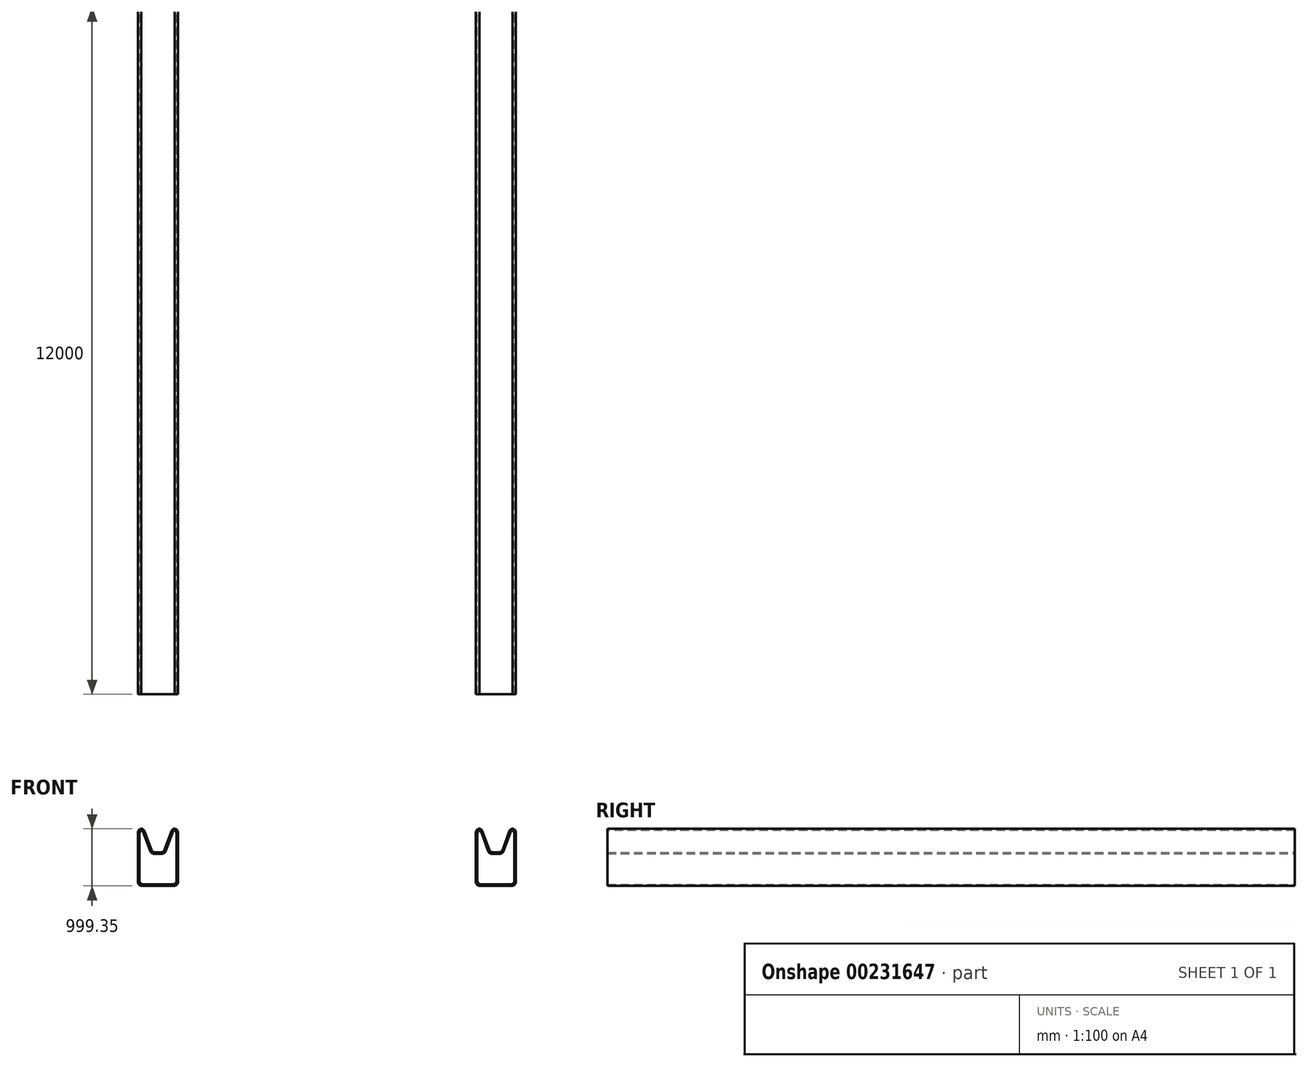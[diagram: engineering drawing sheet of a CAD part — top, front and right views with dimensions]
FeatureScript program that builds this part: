
annotation { "Feature Type Name" : "Feature", "Feature Type Description" : "" }
export const myFeature = defineFeature(function(context is Context, id is Id, definition is map)
    precondition{}
    {
        {
            var Q0;
            Q0=qCreatedBy(makeId("Front.planeOp"),FACE);
            var sketch = newSketch(context, id + "F0", { "sketchPlane" : qUnion([Q0])});
            skLineSegment(sketch, "E0.bottom", {"start": v(2600, 500) * mm, "end": v(2700, 500) * mm});
            skLineSegment(sketch, "E0.top", {"start": v(2600, -500) * mm, "end": v(3300, -500) * mm});
            skLineSegment(sketch, "E0.left", {"start": v(2600, 500) * mm, "end": v(2600, 200) * mm});
            skLineSegment(sketch, "E0.right", {"start": v(3300, 500) * mm, "end": v(3300, -500) * mm});
            skLineSegment(sketch, "E1", {"start": v(0, 0) * mm, "end": v(0, 1224.09) * mm, "construction": true});
            skLineSegment(sketch, "E2", {"start": v(2600, 200) * mm, "end": v(2600, 0) * mm});
            skLineSegment(sketch, "E3", {"start": v(2600, 0) * mm, "end": v(2600, -200) * mm});
            skLineSegment(sketch, "E4", {"start": v(2600, -200) * mm, "end": v(2600, -200) * mm});
            skLineSegment(sketch, "E5.trimOffspring", {"start": v(2600, -200) * mm, "end": v(2600, -500) * mm});
            skLineSegment(sketch, "E6", {"start": v(2700, 500) * mm, "end": v(2850, 87.88) * mm});
            skLineSegment(sketch, "E7", {"start": v(2850, 87.88) * mm, "end": v(3050, 87.88) * mm});
            skLineSegment(sketch, "E8", {"start": v(3050, 87.88) * mm, "end": v(3200, 500) * mm});
            skLineSegment(sketch, "E9.trimOffspring", {"start": v(3200, 500) * mm, "end": v(3300, 500) * mm});
            skLineSegment(sketch, "E10.MirrorCS", {"start": v(-2600, 0) * mm, "end": v(-2600, -200) * mm});
            skLineSegment(sketch, "E11.MirrorCS", {"start": v(-3200, 500) * mm, "end": v(-3300, 500) * mm});
            skLineSegment(sketch, "E12.MirrorCS", {"start": v(-3050, 87.88) * mm, "end": v(-3200, 500) * mm});
            skLineSegment(sketch, "E13.MirrorCS", {"start": v(-2850, 87.88) * mm, "end": v(-3050, 87.88) * mm});
            skLineSegment(sketch, "E14.MirrorCS", {"start": v(-2700, 500) * mm, "end": v(-2850, 87.88) * mm});
            skLineSegment(sketch, "E15.MirrorCS", {"start": v(-2600, 200) * mm, "end": v(-2600, 0) * mm});
            skLineSegment(sketch, "E16.MirrorCS", {"start": v(-2600, 500) * mm, "end": v(-2700, 500) * mm});
            skLineSegment(sketch, "E17.MirrorCS", {"start": v(-2600, -200) * mm, "end": v(-2600, -500) * mm});
            skLineSegment(sketch, "E18.MirrorCS", {"start": v(-3300, 500) * mm, "end": v(-3300, -500) * mm});
            skLineSegment(sketch, "E19.MirrorCS", {"start": v(-2600, -500) * mm, "end": v(-3300, -500) * mm});
            skLineSegment(sketch, "E20.MirrorCS", {"start": v(-2600, 500) * mm, "end": v(-2600, 200) * mm});
            skSolve(sketch);
        }
        {
            var Q0;
            Q0=makeQuery(id+"F0.imprint","IMPRINT",FACE,{"disambiguationData":[TD([[makeQuery(id+"F0.imprint","IMPRINT",EDGE,{"derivedFrom":sQuery(id+"F0.wireOp",EDGE,"918bb700-47ec-41b8-abfe-305a6231168f0.MirrorCS")}),1.0]])]});
            var Q1;
            Q1=makeQuery(id+"F0.imprint","IMPRINT",FACE,{"disambiguationData":[TD([[makeQuery(id+"F0.imprint","IMPRINT",EDGE,{"derivedFrom":sQuery(id+"F0.wireOp",EDGE,"E0.bottom")}),-1.0]])]});
            var Q2;
            Q2=makeQuery(id+"F0.imprint","IMPRINT",FACE,{"disambiguationData":[TD([[makeQuery(id+"F0.imprint","IMPRINT",EDGE,{"derivedFrom":sQuery(id+"F0.wireOp",EDGE,"ff181479-e5d5-4ab7-ba74-e448b7463ad31.MirrorCS")}),-1.0]])]});
            var Q3;
            Q3=makeQuery(id+"F0.imprint","IMPRINT",FACE,{"disambiguationData":[TD([[makeQuery(id+"F0.imprint","IMPRINT",EDGE,{"derivedFrom":sQuery(id+"F0.wireOp",EDGE,"E10.MirrorCS")}),-1.0]])]});
            extrude(context, id + "F1", {"entities" : qUnion([Q0, Q1, Q2, Q3]), "endBound" : BoundingType.SYMMETRIC, "depth" : 12000 * mm});
        }
        {
            var Q0;
            Q0=makeQuery(id+"F1.opExtrude","CAP_FACE",FACE,{"disambiguationData":[OSD([sQuery(id+"F0.wireOp",EDGE,"918bb700-47ec-41b8-abfe-305a6231168f0.MirrorCS"),sQuery(id+"F0.wireOp",EDGE,"918bb700-47ec-41b8-abfe-305a6231168f1.MirrorCS"),sQuery(id+"F0.wireOp",EDGE,"918bb700-47ec-41b8-abfe-305a6231168f2.MirrorCS"),sQuery(id+"F0.wireOp",EDGE,"918bb700-47ec-41b8-abfe-305a6231168f3.MirrorCS")])],"isStart":false});
            var Q1;
            Q1=makeQuery(id+"F1.opExtrude","CAP_FACE",FACE,{"disambiguationData":[OSD([sQuery(id+"F0.wireOp",EDGE,"E0.bottom"),sQuery(id+"F0.wireOp",EDGE,"E0.top"),sQuery(id+"F0.wireOp",EDGE,"E0.left"),sQuery(id+"F0.wireOp",EDGE,"E0.right")])],"isStart":false});
            var Q2;
            Q2=makeQuery(id+"F1.opExtrude","CAP_FACE",FACE,{"disambiguationData":[OSD([sQuery(id+"F0.wireOp",EDGE,"918bb700-47ec-41b8-abfe-305a6231168f0.MirrorCS"),sQuery(id+"F0.wireOp",EDGE,"918bb700-47ec-41b8-abfe-305a6231168f1.MirrorCS"),sQuery(id+"F0.wireOp",EDGE,"918bb700-47ec-41b8-abfe-305a6231168f2.MirrorCS"),sQuery(id+"F0.wireOp",EDGE,"918bb700-47ec-41b8-abfe-305a6231168f3.MirrorCS")])],"isStart":true});
            var Q3;
            Q3=makeQuery(id+"F1.opExtrude","CAP_FACE",FACE,{"disambiguationData":[OSD([sQuery(id+"F0.wireOp",EDGE,"E0.bottom"),sQuery(id+"F0.wireOp",EDGE,"E0.top"),sQuery(id+"F0.wireOp",EDGE,"E0.left"),sQuery(id+"F0.wireOp",EDGE,"E0.right")])],"isStart":true});
            var Q4;
            Q4=makeQuery(id+"F1.opExtrude","CAP_FACE",FACE,{"disambiguationData":[OSD([sQuery(id+"F0.wireOp",EDGE,"E10.MirrorCS"),sQuery(id+"F0.wireOp",EDGE,"E11.MirrorCS"),sQuery(id+"F0.wireOp",EDGE,"E12.MirrorCS"),sQuery(id+"F0.wireOp",EDGE,"E13.MirrorCS"),sQuery(id+"F0.wireOp",EDGE,"E14.MirrorCS"),sQuery(id+"F0.wireOp",EDGE,"E15.MirrorCS"),sQuery(id+"F0.wireOp",EDGE,"E16.MirrorCS"),sQuery(id+"F0.wireOp",EDGE,"E17.MirrorCS"),sQuery(id+"F0.wireOp",EDGE,"E18.MirrorCS"),sQuery(id+"F0.wireOp",EDGE,"E19.MirrorCS"),sQuery(id+"F0.wireOp",EDGE,"E20.MirrorCS")])],"isStart":false});
            var Q5;
            Q5=makeQuery(id+"F1.opExtrude","CAP_FACE",FACE,{"disambiguationData":[OSD([sQuery(id+"F0.wireOp",EDGE,"E10.MirrorCS"),sQuery(id+"F0.wireOp",EDGE,"E11.MirrorCS"),sQuery(id+"F0.wireOp",EDGE,"E12.MirrorCS"),sQuery(id+"F0.wireOp",EDGE,"E13.MirrorCS"),sQuery(id+"F0.wireOp",EDGE,"E14.MirrorCS"),sQuery(id+"F0.wireOp",EDGE,"E15.MirrorCS"),sQuery(id+"F0.wireOp",EDGE,"E16.MirrorCS"),sQuery(id+"F0.wireOp",EDGE,"E17.MirrorCS"),sQuery(id+"F0.wireOp",EDGE,"E18.MirrorCS"),sQuery(id+"F0.wireOp",EDGE,"E19.MirrorCS"),sQuery(id+"F0.wireOp",EDGE,"E20.MirrorCS")])],"isStart":true});
            shell(context, id + "F2", {"entities" : qUnion([Q0, Q1, Q2, Q3, Q4, Q5]), "thickness" : 26 * mm});
        }
        {
            var Q0;
            Q0=makeQuery(id+"F1.opExtrude","SWEPT_EDGE",EDGE,{"disambiguationData":[OSD([sQuery(id+"F0.wireOp",EDGE,"E0.right"),sQuery(id+"F0.wireOp",EDGE,"E9.trimOffspring")])]});
            var Q1;
            Q1=makeQuery(id+"F1.opExtrude","SWEPT_EDGE",EDGE,{"disambiguationData":[OSD([sQuery(id+"F0.wireOp",EDGE,"E6"),sQuery(id+"F0.wireOp",EDGE,"E7")])]});
            var Q2;
            Q2=makeQuery(id+"F1.opExtrude","SWEPT_EDGE",EDGE,{"disambiguationData":[OSD([sQuery(id+"F0.wireOp",EDGE,"E0.bottom"),sQuery(id+"F0.wireOp",EDGE,"E6")])]});
            var Q3;
            Q3=makeQuery(id+"F1.opExtrude","SWEPT_EDGE",EDGE,{"disambiguationData":[OSD([sQuery(id+"F0.wireOp",EDGE,"E0.bottom"),sQuery(id+"F0.wireOp",EDGE,"E0.left")])]});
            var Q4;
            Q4=makeQuery(id+"F1.opExtrude","SWEPT_EDGE",EDGE,{"disambiguationData":[OSD([sQuery(id+"F0.wireOp",EDGE,"E8"),sQuery(id+"F0.wireOp",EDGE,"E9.trimOffspring")])]});
            var Q5;
            Q5=makeQuery(id+"F1.opExtrude","SWEPT_EDGE",EDGE,{"disambiguationData":[OSD([sQuery(id+"F0.wireOp",EDGE,"E0.top"),sQuery(id+"F0.wireOp",EDGE,"E0.right")])]});
            var Q6;
            Q6=makeQuery(id+"F2.opShell","OFFSET_EDGE",EDGE,{"disambiguationData":[OSD([sQuery(id+"F0.wireOp",EDGE,"E0.top"),sQuery(id+"F0.wireOp",EDGE,"E5.trimOffspring")])]});
            var Q7;
            Q7=makeQuery(id+"F2.opShell","OFFSET_EDGE",EDGE,{"disambiguationData":[OSD([sQuery(id+"F0.wireOp",EDGE,"E8"),sQuery(id+"F0.wireOp",EDGE,"E9.trimOffspring")])]});
            var Q8;
            Q8=makeQuery(id+"F2.opShell","OFFSET_EDGE",EDGE,{"disambiguationData":[OSD([sQuery(id+"F0.wireOp",EDGE,"E7"),sQuery(id+"F0.wireOp",EDGE,"E8")])]});
            var Q9;
            Q9=makeQuery(id+"F2.opShell","OFFSET_EDGE",EDGE,{"disambiguationData":[OSD([sQuery(id+"F0.wireOp",EDGE,"E0.right"),sQuery(id+"F0.wireOp",EDGE,"E9.trimOffspring")])]});
            var Q10;
            Q10=makeQuery(id+"F2.opShell","OFFSET_EDGE",EDGE,{"disambiguationData":[OSD([sQuery(id+"F0.wireOp",EDGE,"E0.bottom"),sQuery(id+"F0.wireOp",EDGE,"E6")])]});
            var Q11;
            Q11=makeQuery(id+"F2.opShell","OFFSET_EDGE",EDGE,{"disambiguationData":[OSD([sQuery(id+"F0.wireOp",EDGE,"E6"),sQuery(id+"F0.wireOp",EDGE,"E7")])]});
            var Q12;
            Q12=makeQuery(id+"F2.opShell","OFFSET_EDGE",EDGE,{"disambiguationData":[OSD([sQuery(id+"F0.wireOp",EDGE,"E0.bottom"),sQuery(id+"F0.wireOp",EDGE,"E0.left")])]});
            var Q13;
            Q13=makeQuery(id+"F1.opExtrude","SWEPT_EDGE",EDGE,{"disambiguationData":[OSD([sQuery(id+"F0.wireOp",EDGE,"E0.top"),sQuery(id+"F0.wireOp",EDGE,"E5.trimOffspring")])]});
            var Q14;
            Q14=makeQuery(id+"F2.opShell","OFFSET_EDGE",EDGE,{"disambiguationData":[OSD([sQuery(id+"F0.wireOp",EDGE,"E0.top"),sQuery(id+"F0.wireOp",EDGE,"E0.right")])]});
            var Q15;
            Q15=makeQuery(id+"F1.opExtrude","SWEPT_EDGE",EDGE,{"disambiguationData":[OSD([sQuery(id+"F0.wireOp",EDGE,"E7"),sQuery(id+"F0.wireOp",EDGE,"E8")])]});
            fillet(context, id + "F3", {"entities" : qUnion([Q0, Q1, Q2, Q3, Q4, Q5, Q6, Q7, Q8, Q9, Q10, Q11, Q12, Q13, Q14, Q15]), "radius" : 70 * mm, "tangentPropagation" : true, "allowEdgeOverflow" : false});
        }
        {
            var Q0;
            Q0=makeQuery(id+"F1.opExtrude","SWEPT_EDGE",EDGE,{"disambiguationData":[OSD([sQuery(id+"F0.wireOp",EDGE,"E16.MirrorCS"),sQuery(id+"F0.wireOp",EDGE,"E20.MirrorCS")])]});
            var Q1;
            Q1=makeQuery(id+"F1.opExtrude","SWEPT_EDGE",EDGE,{"disambiguationData":[OSD([sQuery(id+"F0.wireOp",EDGE,"E14.MirrorCS"),sQuery(id+"F0.wireOp",EDGE,"E16.MirrorCS")])]});
            var Q2;
            Q2=makeQuery(id+"F1.opExtrude","SWEPT_EDGE",EDGE,{"disambiguationData":[OSD([sQuery(id+"F0.wireOp",EDGE,"E12.MirrorCS"),sQuery(id+"F0.wireOp",EDGE,"E13.MirrorCS")])]});
            var Q3;
            Q3=makeQuery(id+"F1.opExtrude","SWEPT_EDGE",EDGE,{"disambiguationData":[OSD([sQuery(id+"F0.wireOp",EDGE,"E11.MirrorCS"),sQuery(id+"F0.wireOp",EDGE,"E12.MirrorCS")])]});
            var Q4;
            Q4=makeQuery(id+"F1.opExtrude","SWEPT_EDGE",EDGE,{"disambiguationData":[OSD([sQuery(id+"F0.wireOp",EDGE,"E11.MirrorCS"),sQuery(id+"F0.wireOp",EDGE,"E18.MirrorCS")])]});
            var Q5;
            Q5=makeQuery(id+"F2.opShell","OFFSET_EDGE",EDGE,{"disambiguationData":[OSD([sQuery(id+"F0.wireOp",EDGE,"E13.MirrorCS"),sQuery(id+"F0.wireOp",EDGE,"E14.MirrorCS")])]});
            var Q6;
            Q6=makeQuery(id+"F1.opExtrude","SWEPT_EDGE",EDGE,{"disambiguationData":[OSD([sQuery(id+"F0.wireOp",EDGE,"E17.MirrorCS"),sQuery(id+"F0.wireOp",EDGE,"E19.MirrorCS")])]});
            var Q7;
            Q7=makeQuery(id+"F2.opShell","OFFSET_EDGE",EDGE,{"disambiguationData":[OSD([sQuery(id+"F0.wireOp",EDGE,"E18.MirrorCS"),sQuery(id+"F0.wireOp",EDGE,"E19.MirrorCS")])]});
            var Q8;
            Q8=makeQuery(id+"F2.opShell","OFFSET_EDGE",EDGE,{"disambiguationData":[OSD([sQuery(id+"F0.wireOp",EDGE,"E17.MirrorCS"),sQuery(id+"F0.wireOp",EDGE,"E19.MirrorCS")])]});
            var Q9;
            Q9=makeQuery(id+"F1.opExtrude","SWEPT_EDGE",EDGE,{"disambiguationData":[OSD([sQuery(id+"F0.wireOp",EDGE,"E13.MirrorCS"),sQuery(id+"F0.wireOp",EDGE,"E14.MirrorCS")])]});
            var Q10;
            Q10=makeQuery(id+"F2.opShell","OFFSET_EDGE",EDGE,{"disambiguationData":[OSD([sQuery(id+"F0.wireOp",EDGE,"E11.MirrorCS"),sQuery(id+"F0.wireOp",EDGE,"E12.MirrorCS")])]});
            var Q11;
            Q11=makeQuery(id+"F2.opShell","OFFSET_EDGE",EDGE,{"disambiguationData":[OSD([sQuery(id+"F0.wireOp",EDGE,"E12.MirrorCS"),sQuery(id+"F0.wireOp",EDGE,"E13.MirrorCS")])]});
            var Q12;
            Q12=makeQuery(id+"F2.opShell","OFFSET_EDGE",EDGE,{"disambiguationData":[OSD([sQuery(id+"F0.wireOp",EDGE,"E14.MirrorCS"),sQuery(id+"F0.wireOp",EDGE,"E16.MirrorCS")])]});
            var Q13;
            Q13=makeQuery(id+"F2.opShell","OFFSET_EDGE",EDGE,{"disambiguationData":[OSD([sQuery(id+"F0.wireOp",EDGE,"E16.MirrorCS"),sQuery(id+"F0.wireOp",EDGE,"E20.MirrorCS")])]});
            var Q14;
            Q14=makeQuery(id+"F2.opShell","OFFSET_EDGE",EDGE,{"disambiguationData":[OSD([sQuery(id+"F0.wireOp",EDGE,"E11.MirrorCS"),sQuery(id+"F0.wireOp",EDGE,"E18.MirrorCS")])]});
            var Q15;
            Q15=makeQuery(id+"F1.opExtrude","SWEPT_EDGE",EDGE,{"disambiguationData":[OSD([sQuery(id+"F0.wireOp",EDGE,"E18.MirrorCS"),sQuery(id+"F0.wireOp",EDGE,"E19.MirrorCS")])]});
            fillet(context, id + "F4", {"entities" : qUnion([Q0, Q1, Q2, Q3, Q4, Q5, Q6, Q7, Q8, Q9, Q10, Q11, Q12, Q13, Q14, Q15]), "radius" : 70 * mm, "tangentPropagation" : true, "allowEdgeOverflow" : false});
        }
    });
